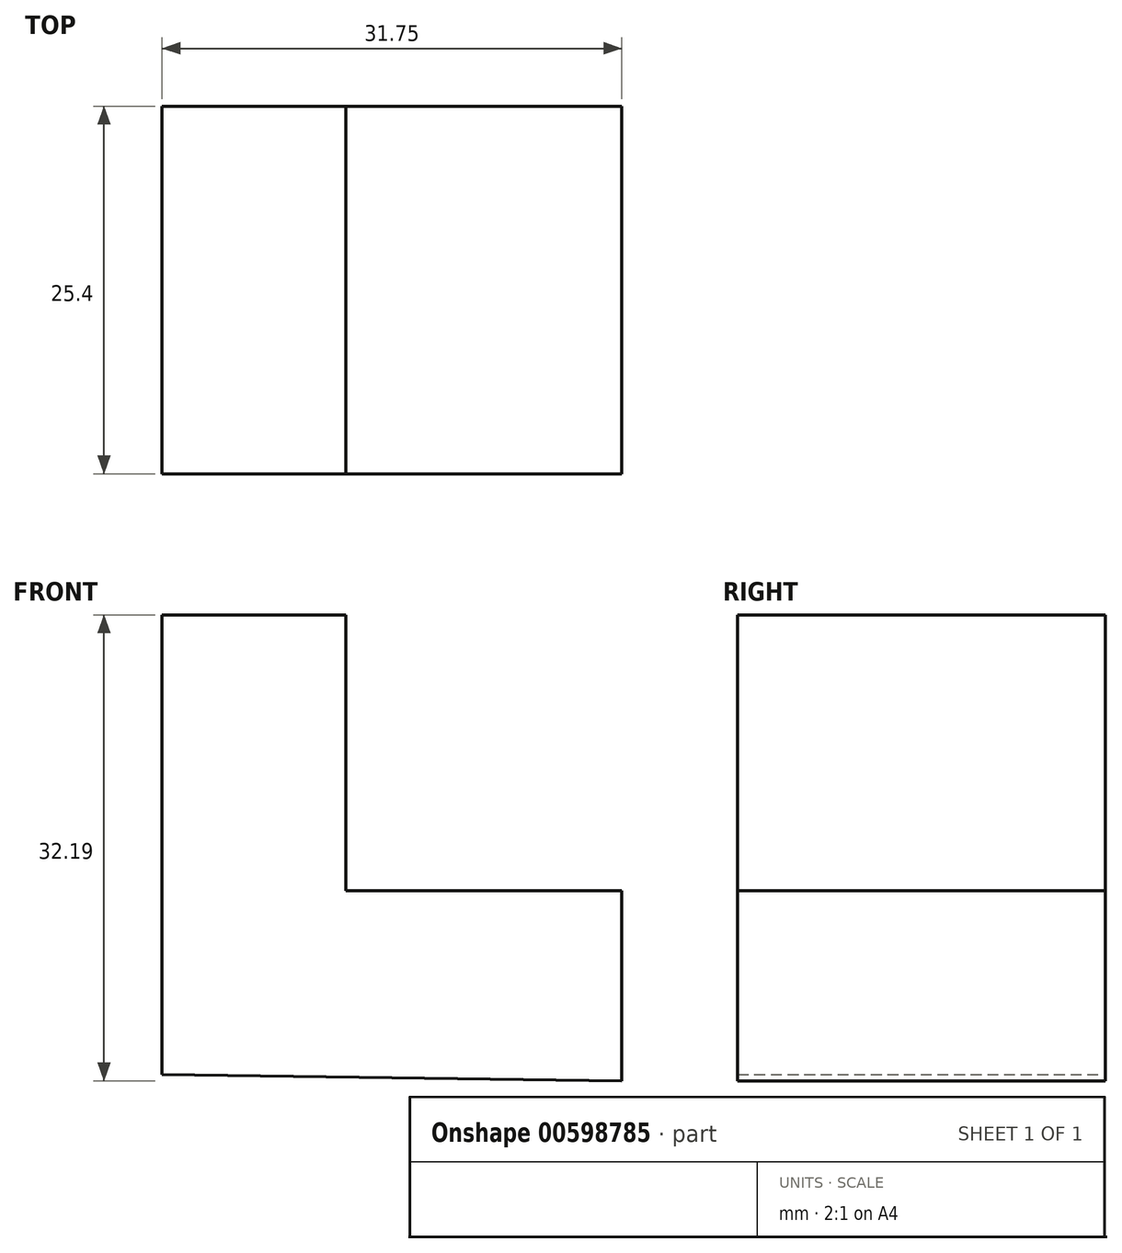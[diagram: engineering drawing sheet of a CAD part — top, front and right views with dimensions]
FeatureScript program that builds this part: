
annotation { "Feature Type Name" : "Feature", "Feature Type Description" : "" }
export const myFeature = defineFeature(function(context is Context, id is Id, definition is map)
    precondition{}
    {
        {
            var Q0;
            Q0=qCreatedBy(makeId("Front.planeOp"),FACE);
            var sketch = newSketch(context, id + "F0", { "sketchPlane" : qUnion([Q0])});
            skLineSegment(sketch, "E0", {"start": v(0, 0.44) * mm, "end": v(0, 0) * mm});
            skLineSegment(sketch, "E1", {"start": v(0, 0.44) * mm, "end": v(0, 32.19) * mm});
            skLineSegment(sketch, "E2", {"start": v(0, 32.19) * mm, "end": v(12.7, 32.19) * mm});
            skLineSegment(sketch, "E3", {"start": v(12.7, 32.19) * mm, "end": v(12.7, 13.14) * mm});
            skLineSegment(sketch, "E4", {"start": v(12.7, 13.14) * mm, "end": v(31.75, 13.14) * mm});
            skLineSegment(sketch, "E5", {"start": v(31.75, 13.14) * mm, "end": v(31.75, 0) * mm});
            skLineSegment(sketch, "E6", {"start": v(31.75, 0) * mm, "end": v(0, 0.44) * mm});
            skSolve(sketch);
        }
        {
            var Q0;
            Q0 = qSketchRegion(id + "F0", true);
            extrude(context, id + "F1", {"entities" : qUnion([Q0]), "depth" : 25.4 * mm, "offsetDistance" : 25.4 * mm});
        }
    });
